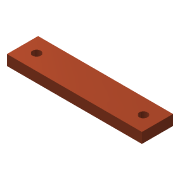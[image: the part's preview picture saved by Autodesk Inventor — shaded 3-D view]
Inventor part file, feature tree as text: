
AUTODESK INVENTOR PART (.ipt)
format: ipt  version: 2016 SP2 (Build 200236200, 236)  size: 90,112 bytes
history: native  units: mm
features: sketch x2, extrude x1, hole x1
ambient origin geometry x8: Origin, YZ Plane, XZ Plane, XY Plane, X Axis, Y Axis, Z Axis, Center Point
bodies: Body1 (feature_tree)
feature tree (4):
  extrude  "Extrusion3"  Depth=30.0mm
  hole  "Hole1"  [1 undecoded]
  sketch  "Sketch1"  dims[d4=130.0mm d5=30.0mm]
  sketch  "Sketch2"  dims[d6=10.0mm d7=0.0mm d8=101.8mm d9=50.9mm d10=8.2mm d11=6.0mm d12=4.0mm d13=2.0mm d14=90.0deg d15=8.0mm d16=20.594885mm]
note: 1 required parameter value undecoded (feature->parameter linkage not recoverable at this tier; creation-order binding heuristic only, values carry confidence <= 0.55)
